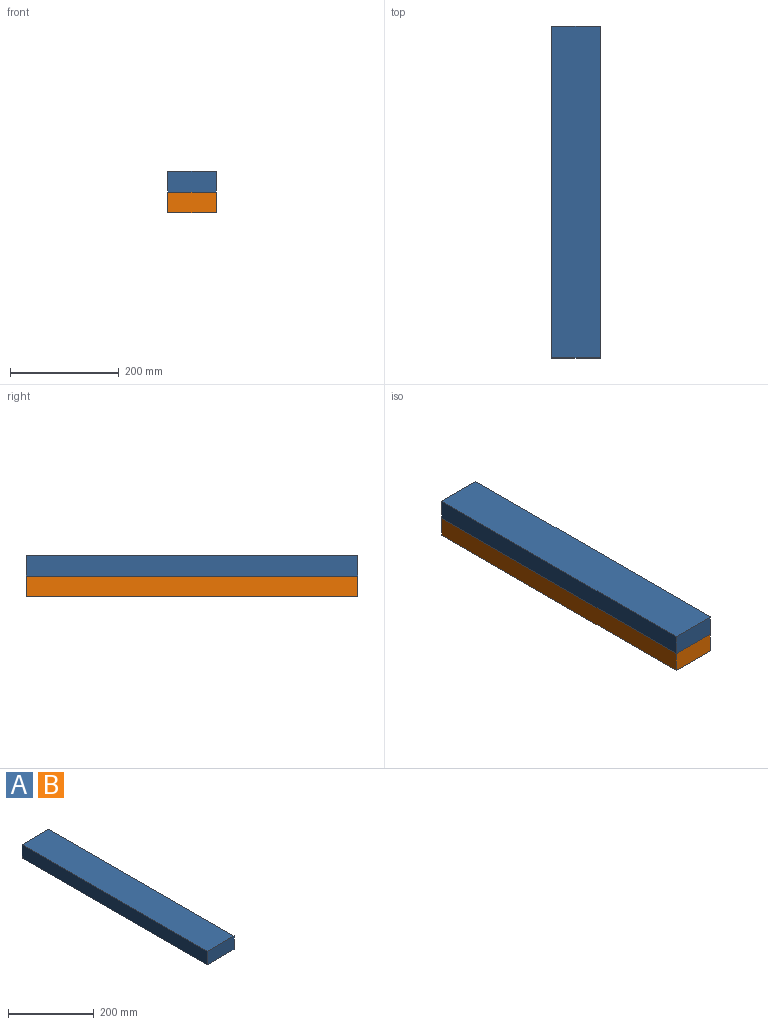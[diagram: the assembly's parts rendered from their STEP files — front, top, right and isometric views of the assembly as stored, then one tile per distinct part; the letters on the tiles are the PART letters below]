
ASSEMBLY  parts=2 mates=1
PART A: 6 faces, bbox 88.9x609.6x38.1 mm
  f0: plane 609.6x88.9mm, normal (0,0,-1), area 54193.4mm2, adj f1,f3,f4,f5
  f1: plane 609.6x38.1mm, normal (1,0,0), area 23225.8mm2, adj f0,f2,f4,f5
  f2: plane 609.6x88.9mm, normal (0,0,1), area 54193.4mm2, adj f1,f3,f4,f5
  f3: plane 609.6x38.1mm, normal (-1,0,0), area 23225.8mm2, adj f0,f2,f4,f5
  f4: plane 88.9x38.1mm, normal (0,-1,0), area 3387.1mm2, adj f0,f1,f2,f3
  f5: plane 88.9x38.1mm, normal (0,1,0), area 3387.1mm2, adj f0,f1,f2,f3
PART B: same geometry as A
PLACE A t=(0,304.8,57.15)mm
PLACE B t=(0,304.8,19.05)mm
MATE fastened B.f2 <-> A.f0  axis (0,0,1) through (0,0,38.1)mm
